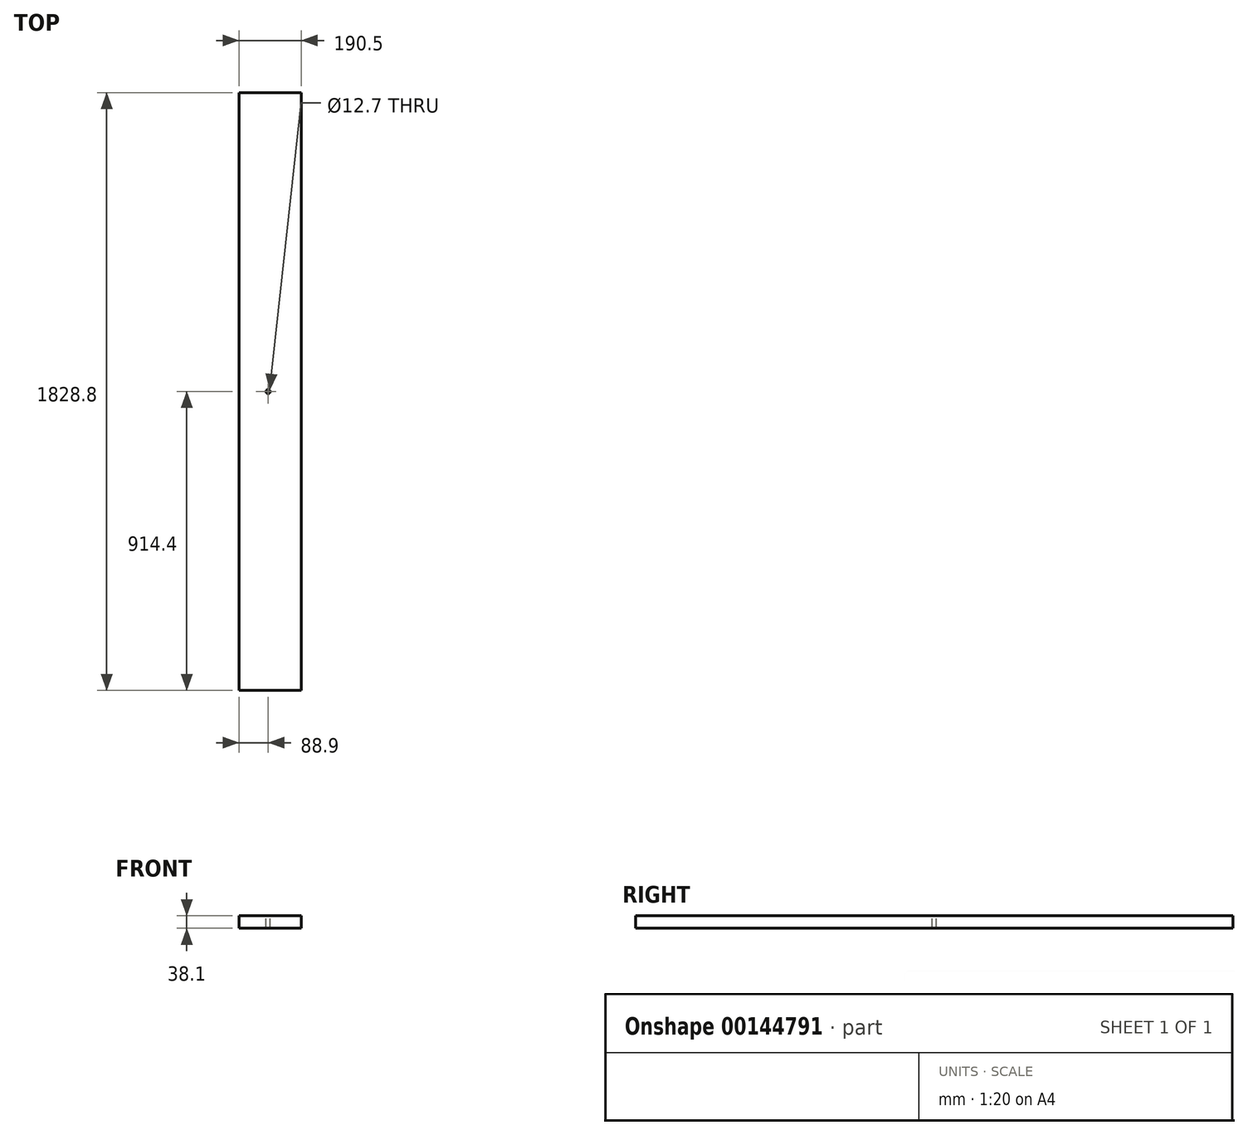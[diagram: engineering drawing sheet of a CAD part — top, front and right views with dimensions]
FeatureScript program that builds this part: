
annotation { "Feature Type Name" : "Feature", "Feature Type Description" : "" }
export const myFeature = defineFeature(function(context is Context, id is Id, definition is map)
    precondition{}
    {
        {
            var Q0;
            Q0=qCreatedBy(makeId("Front.planeOp"),FACE);
            var sketch = newSketch(context, id + "F0", { "sketchPlane" : qUnion([Q0])});
            skLineSegment(sketch, "E0.bottom", {"start": v(0, 0) * mm, "end": v(190.5, 0) * mm});
            skLineSegment(sketch, "E0.top", {"start": v(0, 38.1) * mm, "end": v(190.5, 38.1) * mm});
            skLineSegment(sketch, "E0.left", {"start": v(0, 0) * mm, "end": v(0, 38.1) * mm});
            skLineSegment(sketch, "E0.right", {"start": v(190.5, 0) * mm, "end": v(190.5, 38.1) * mm});
            skSolve(sketch);
        }
        {
            var Q0;
            Q0=makeQuery(id+"F0.imprint","IMPRINT",FACE,{"disambiguationData":[TD([[makeQuery(id+"F0.imprint","IMPRINT",EDGE,{"derivedFrom":sQuery(id+"F0.wireOp",EDGE,"E0.bottom")}),1.0]])]});
            extrude(context, id + "F1", {"entities" : qUnion([Q0]), "depth" : 1828.8 * mm});
        }
        {
            var Q0;
            Q0=makeQuery(id+"F1.opExtrude","SWEPT_FACE",FACE,{"disambiguationData":[OSD([sQuery(id+"F0.wireOp",EDGE,"E0.top")])]});
            var sketch = newSketch(context, id + "F2", { "sketchPlane" : qUnion([Q0])});
            skCircle(sketch, "E1", {"center": v(88.9, -914.4) * mm, "radius": 6.35 * mm});
            skSolve(sketch);
        }
        {
            var Q0;
            Q0 = qSketchRegion(id + "F2", true);
            extrude(context, id + "F3", {"entities" : qUnion([Q0]), "operationType" : NewBodyOperationType.REMOVE, "endBound" : BoundingType.THROUGH_ALL, "oppositeDirection" : true, "depth" : 25.4 * mm});
        }
    });
